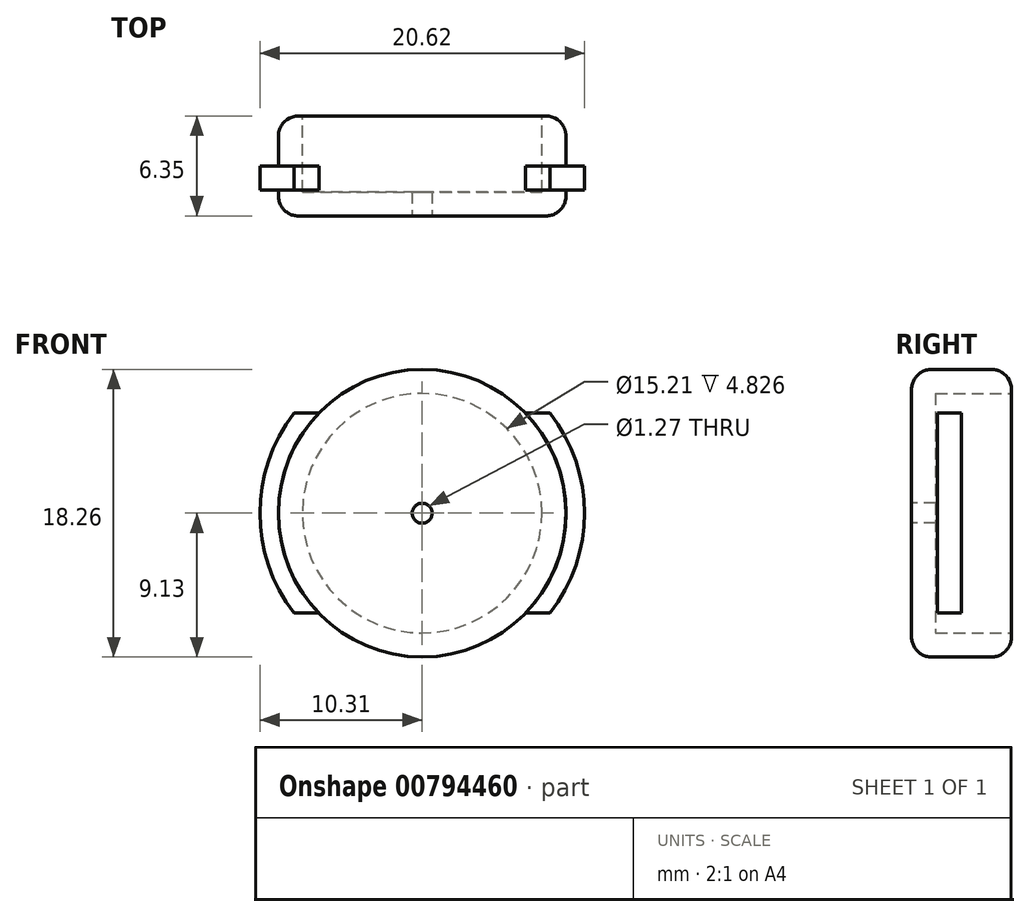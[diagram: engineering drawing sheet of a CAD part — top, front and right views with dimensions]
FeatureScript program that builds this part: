
annotation { "Feature Type Name" : "Feature", "Feature Type Description" : "" }
export const myFeature = defineFeature(function(context is Context, id is Id, definition is map)
    precondition{}
    {
        {
            var Q0;
            Q0=qCreatedBy(makeId("Front.planeOp"),FACE);
            var sketch = newSketch(context, id + "F0", { "sketchPlane" : qUnion([Q0])});
            skCircle(sketch, "E0", {"center": v(0, 0) * mm, "radius": 9.13 * mm});
            skSolve(sketch);
        }
        {
            var Q0;
            Q0 = qSketchRegion(id + "F0", true);
            extrude(context, id + "F1", {"entities" : qUnion([Q0]), "depth" : 3.17 * mm, "offsetDistance" : 25.4 * mm});
        }
        {
            var Q0;
            Q0=makeQuery(id+"F1.opExtrude","CAP_FACE",FACE,{"disambiguationData":[OSD([sQuery(id+"F0.wireOp",EDGE,"E0")])],"isStart":false});
            var sketch = newSketch(context, id + "F2", { "sketchPlane" : qUnion([Q0])});
            skArc(sketch, "E1", {"start": v(-8.13, 6.35) * mm, "mid": v(-10.31, 0) * mm, "end": v(-8.13, -6.35) * mm});
            skLineSegment(sketch, "E2", {"start": v(-8.13, 6.35) * mm, "end": v(8.13, 6.35) * mm});
            skLineSegment(sketch, "E3", {"start": v(-8.13, 6.35) * mm, "end": v(-8.13, -6.35) * mm, "construction": true});
            skLineSegment(sketch, "E4", {"start": v(8.13, 6.35) * mm, "end": v(8.13, -6.35) * mm, "construction": true});
            skLineSegment(sketch, "E5", {"start": v(-8.13, -6.35) * mm, "end": v(8.13, -6.35) * mm});
            skArc(sketch, "E6.trimOffspring", {"start": v(8.13, -6.35) * mm, "mid": v(10.31, 0) * mm, "end": v(8.13, 6.35) * mm});
            skSolve(sketch);
        }
        {
            var Q0;
            Q0 = qSketchRegion(id + "F2", true);
            extrude(context, id + "F3", {"entities" : qUnion([Q0]), "operationType" : NewBodyOperationType.ADD, "depth" : 1.52 * mm, "offsetDistance" : 25.4 * mm});
        }
        {
            var Q0;
            Q0=makeQuery(id+"F3.opExtrude","CAP_FACE",FACE,{"disambiguationData":[OSD([sQuery(id+"F2.wireOp",EDGE,"E1"),sQuery(id+"F2.wireOp",EDGE,"E2"),sQuery(id+"F2.wireOp",EDGE,"E5"),sQuery(id+"F2.wireOp",EDGE,"E6.trimOffspring")])],"isStart":false});
            var sketch = newSketch(context, id + "F4", { "sketchPlane" : qUnion([Q0])});
            skCircle(sketch, "E7", {"center": v(0, 0) * mm, "radius": 9.13 * mm});
            skSolve(sketch);
        }
        {
            var Q0;
            Q0 = qSketchRegion(id + "F4", true);
            extrude(context, id + "F5", {"entities" : qUnion([Q0]), "operationType" : NewBodyOperationType.ADD, "oppositeDirection" : true, "depth" : 1.52 * mm, "offsetDistance" : 25.4 * mm});
        }
        {
            var Q0;
            Q0=makeQuery(id+"F5.boolean.opBoolean","MERGE",FACE,{"derivedFrom":[makeQuery(id+"F3.opExtrude","CAP_FACE",FACE,{"disambiguationData":[OSD([sQuery(id+"F2.wireOp",EDGE,"E1"),sQuery(id+"F2.wireOp",EDGE,"E2"),sQuery(id+"F2.wireOp",EDGE,"E5"),sQuery(id+"F2.wireOp",EDGE,"E6.trimOffspring")])],"isStart":false}),makeQuery(id+"F5.opExtrude","CAP_FACE",FACE,{"disambiguationData":[OSD([sQuery(id+"F4.wireOp",EDGE,"E7")])],"isStart":true})]});
            var sketch = newSketch(context, id + "F6", { "sketchPlane" : qUnion([Q0])});
            skCircle(sketch, "E8", {"center": v(0, 0) * mm, "radius": 9.13 * mm});
            skSolve(sketch);
        }
        {
            var Q0;
            Q0 = qSketchRegion(id + "F6", true);
            extrude(context, id + "F7", {"entities" : qUnion([Q0]), "operationType" : NewBodyOperationType.ADD, "depth" : 1.65 * mm, "offsetDistance" : 25.4 * mm});
        }
        {
            var Q0;
            Q0=makeQuery(id+"F1.opExtrude","CAP_FACE",FACE,{"disambiguationData":[OSD([sQuery(id+"F0.wireOp",EDGE,"E0")])],"isStart":true});
            var sketch = newSketch(context, id + "F8", { "sketchPlane" : qUnion([Q0])});
            skCircle(sketch, "E9", {"center": v(0, 0) * mm, "radius": 7.6 * mm});
            skSolve(sketch);
        }
        {
            var Q0;
            Q0 = qSketchRegion(id + "F8", true);
            extrude(context, id + "F9", {"entities" : qUnion([Q0]), "operationType" : NewBodyOperationType.REMOVE, "oppositeDirection" : true, "depth" : 4.83 * mm, "offsetDistance" : 25.4 * mm});
        }
        {
            var Q0;
            Q0=makeQuery(id+"F7.opExtrude","CAP_FACE",FACE,{"disambiguationData":[OSD([sQuery(id+"F6.wireOp",EDGE,"E8")])],"isStart":false});
            var sketch = newSketch(context, id + "F10", { "sketchPlane" : qUnion([Q0])});
            skCircle(sketch, "E10", {"center": v(0, 0) * mm, "radius": 0.64 * mm});
            skSolve(sketch);
        }
        {
            var Q0;
            Q0 = qSketchRegion(id + "F10", true);
            extrude(context, id + "F11", {"entities" : qUnion([Q0]), "operationType" : NewBodyOperationType.REMOVE, "oppositeDirection" : true, "depth" : 25.4 * mm, "offsetDistance" : 25.4 * mm, "hasSecondDirection" : true, "secondDirectionOppositeDirection" : false, "secondDirectionDepth" : 25.4 * mm});
        }
        {
            var Q0;
            Q0=makeQuery(id+"F7.opExtrude","CAP_EDGE",EDGE,{"disambiguationData":[OSD([sQuery(id+"F6.wireOp",EDGE,"E8")])],"isStart":false});
            fillet(context, id + "F12", {"entities" : qUnion([Q0]), "radius" : 1.27 * mm, "tangentPropagation" : true, "allowEdgeOverflow" : false});
        }
        {
            var Q0;
            Q0=makeQuery(id+"F1.opExtrude","CAP_EDGE",EDGE,{"disambiguationData":[OSD([sQuery(id+"F0.wireOp",EDGE,"E0")])],"isStart":true});
            fillet(context, id + "F13", {"entities" : qUnion([Q0]), "radius" : 1.27 * mm, "tangentPropagation" : true, "allowEdgeOverflow" : false});
        }
    });
